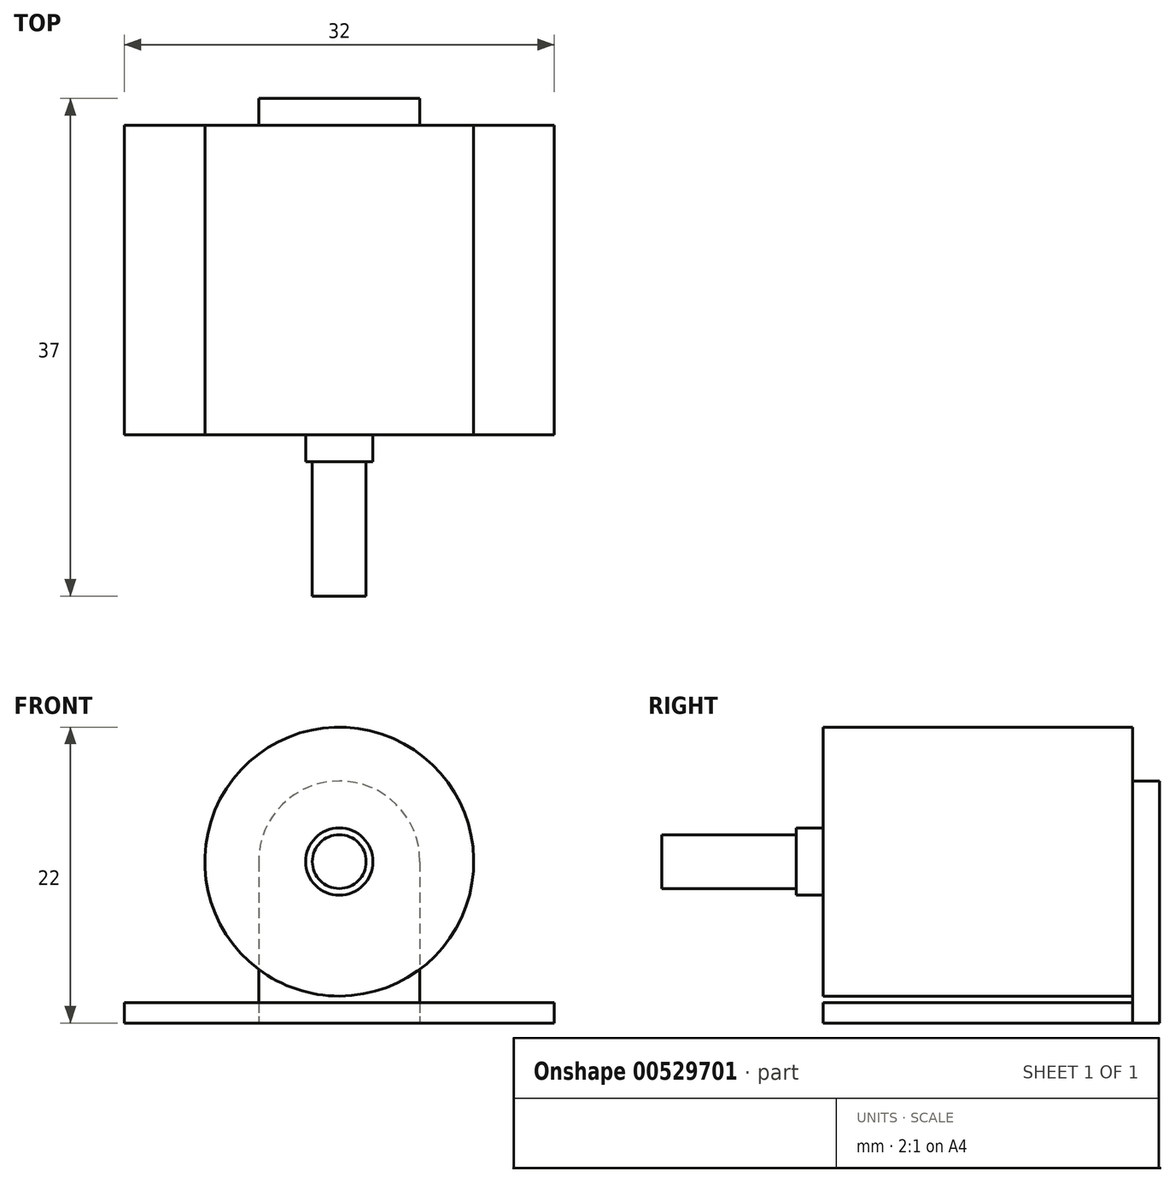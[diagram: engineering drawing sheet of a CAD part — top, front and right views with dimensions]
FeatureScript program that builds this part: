
annotation { "Feature Type Name" : "Feature", "Feature Type Description" : "" }
export const myFeature = defineFeature(function(context is Context, id is Id, definition is map)
    precondition{}
    {
        {
            var Q0;
            Q0=qCreatedBy(makeId("Front.planeOp"),FACE);
            var sketch = newSketch(context, id + "F0", { "sketchPlane" : qUnion([Q0])});
            skCircle(sketch, "E0", {"center": v(0, 12) * mm, "radius": 10 * mm});
            skLineSegment(sketch, "E1.bottom", {"start": v(-16, 0) * mm, "end": v(16, 0) * mm});
            skLineSegment(sketch, "E1.top", {"start": v(-16, 1.5) * mm, "end": v(16, 1.5) * mm});
            skLineSegment(sketch, "E1.left", {"start": v(-16, 1.5) * mm, "end": v(-16, 0) * mm});
            skLineSegment(sketch, "E1.right", {"start": v(16, 1.5) * mm, "end": v(16, 0) * mm});
            skSolve(sketch);
        }
        {
            var Q0;
            Q0 = qSketchRegion(id + "F0", true);
            var Q1;
            Q1=sQuery(id+"F0.wireOp",EDGE,"E0");
            var Q2;
            Q2=sQuery(id+"F0.wireOp",EDGE,"E1.bottom");
            var Q3;
            Q3=sQuery(id+"F0.wireOp",EDGE,"E1.top");
            var Q4;
            Q4=sQuery(id+"F0.wireOp",EDGE,"E1.left");
            var Q5;
            Q5=sQuery(id+"F0.wireOp",EDGE,"E1.right");
            var Q6;
            Q6=sQuery(id+"F0.wireOp",EDGE,"ffa78f30-f037-4124-abd0-8d902fbe385e");
            var Q7;
            Q7=sQuery(id+"F0.wireOp",EDGE,"b4671ef4-4c04-492c-992a-9a2b9d8647ea");
            extrude(context, id + "F1", {"entities" : qUnion([Q0]), "surfaceEntities" : qUnion([Q1, Q2, Q3, Q4, Q5, Q6, Q7]), "depth" : 23 * mm, "offsetDistance" : 25.4 * mm});
        }
        {
            var Q0;
            Q0=makeQuery(id+"F1.opExtrude","CAP_FACE",FACE,{"disambiguationData":[OSD([sQuery(id+"F0.wireOp",EDGE,"E0"),sQuery(id+"F0.wireOp",EDGE,"E1.bottom"),sQuery(id+"F0.wireOp",EDGE,"E1.top"),sQuery(id+"F0.wireOp",EDGE,"E1.left"),sQuery(id+"F0.wireOp",EDGE,"E1.right"),sQuery(id+"F0.wireOp",EDGE,"ffa78f30-f037-4124-abd0-8d902fbe385e"),sQuery(id+"F0.wireOp",EDGE,"b4671ef4-4c04-492c-992a-9a2b9d8647ea")])],"isStart":false});
            var sketch = newSketch(context, id + "F2", { "sketchPlane" : qUnion([Q0])});
            skCircle(sketch, "E2", {"center": v(0, 12) * mm, "radius": 2.5 * mm});
            skSolve(sketch);
        }
        {
            var Q0;
            Q0 = qSketchRegion(id + "F2", true);
            extrude(context, id + "F3", {"entities" : qUnion([Q0]), "operationType" : NewBodyOperationType.ADD, "depth" : 2 * mm, "offsetDistance" : 25 * mm});
        }
        {
            var Q0;
            Q0=makeQuery(id+"F3.opExtrude","CAP_FACE",FACE,{"disambiguationData":[OSD([sQuery(id+"F2.wireOp",EDGE,"E2")])],"isStart":false});
            var sketch = newSketch(context, id + "F4", { "sketchPlane" : qUnion([Q0])});
            skCircle(sketch, "E3", {"center": v(0, 12) * mm, "radius": 2 * mm});
            skSolve(sketch);
        }
        {
            var Q0;
            Q0 = qSketchRegion(id + "F4", true);
            extrude(context, id + "F5", {"entities" : qUnion([Q0]), "operationType" : NewBodyOperationType.ADD, "depth" : 10 * mm, "offsetDistance" : 25 * mm});
        }
        {
            var Q0;
            Q0=makeQuery(id+"F1.opExtrude","CAP_FACE",FACE,{"disambiguationData":[OSD([sQuery(id+"F0.wireOp",EDGE,"E0"),sQuery(id+"F0.wireOp",EDGE,"E1.bottom"),sQuery(id+"F0.wireOp",EDGE,"E1.top"),sQuery(id+"F0.wireOp",EDGE,"E1.left"),sQuery(id+"F0.wireOp",EDGE,"E1.right"),sQuery(id+"F0.wireOp",EDGE,"ffa78f30-f037-4124-abd0-8d902fbe385e"),sQuery(id+"F0.wireOp",EDGE,"b4671ef4-4c04-492c-992a-9a2b9d8647ea")])],"isStart":true});
            var sketch = newSketch(context, id + "F6", { "sketchPlane" : qUnion([Q0])});
            skLineSegment(sketch, "E4.bottom", {"start": v(-6, 12) * mm, "end": v(6, 12) * mm});
            skLineSegment(sketch, "E4.top", {"start": v(-6, 0) * mm, "end": v(6, 0) * mm});
            skLineSegment(sketch, "E4.left", {"start": v(-6, 12) * mm, "end": v(-6, 0) * mm});
            skLineSegment(sketch, "E4.right", {"start": v(6, 12) * mm, "end": v(6, 0) * mm});
            skArc(sketch, "E5", {"start": v(6, 12) * mm, "mid": v(0, 18) * mm, "end": v(-6, 12) * mm});
            skSolve(sketch);
        }
        {
            var Q0;
            Q0 = qSketchRegion(id + "F6", true);
            extrude(context, id + "F7", {"entities" : qUnion([Q0]), "operationType" : NewBodyOperationType.ADD, "depth" : 2 * mm, "offsetDistance" : 25 * mm});
        }
    });
